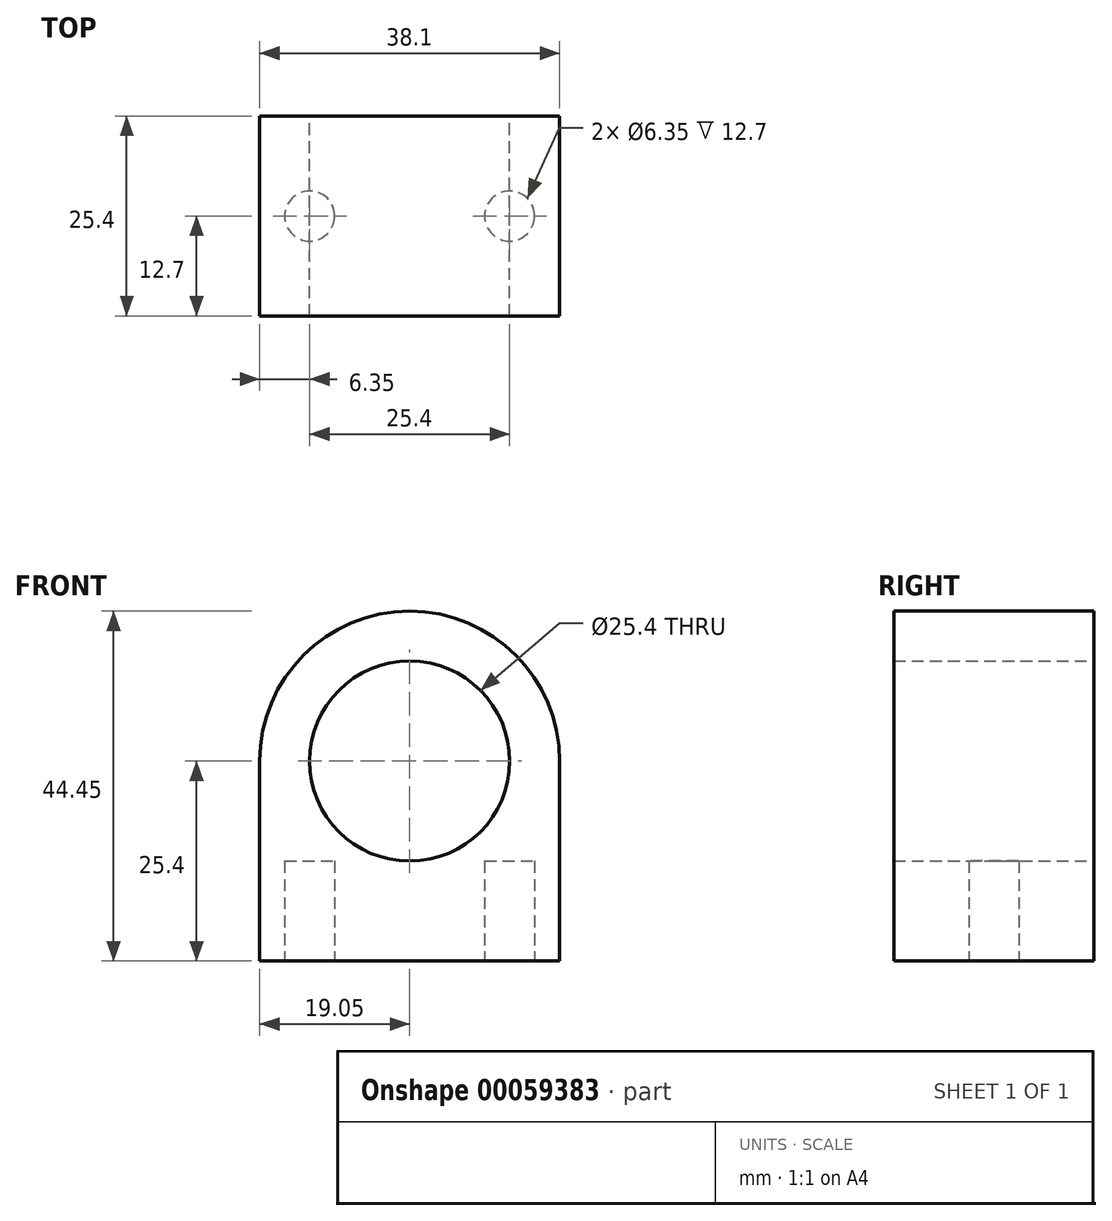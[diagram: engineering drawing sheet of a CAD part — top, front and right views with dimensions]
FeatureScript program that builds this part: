
annotation { "Feature Type Name" : "Feature", "Feature Type Description" : "" }
export const myFeature = defineFeature(function(context is Context, id is Id, definition is map)
    precondition{}
    {
        {
            var Q0;
            Q0=qCreatedBy(makeId("Front.planeOp"),FACE);
            var sketch = newSketch(context, id + "F0", { "sketchPlane" : qUnion([Q0])});
            skLineSegment(sketch, "E0", {"start": v(-52.87, 0) * mm, "end": v(-19.05, 0) * mm, "construction": true});
            skLineSegment(sketch, "E1", {"start": v(0, 60.55) * mm, "end": v(0, -55.86) * mm, "construction": true});
            skCircle(sketch, "E2", {"center": v(0, 25.4) * mm, "radius": 12.7 * mm});
            skArc(sketch, "E3", {"start": v(19.05, 25.4) * mm, "mid": v(0, 44.45) * mm, "end": v(-19.05, 25.4) * mm});
            skLineSegment(sketch, "E4", {"start": v(-19.05, 25.4) * mm, "end": v(-19.05, 0) * mm});
            skLineSegment(sketch, "E5", {"start": v(19.05, 25.4) * mm, "end": v(19.05, 0) * mm});
            skLineSegment(sketch, "E6.trimOffspring", {"start": v(0, 0) * mm, "end": v(57.82, 0) * mm, "construction": true});
            skLineSegment(sketch, "E7", {"start": v(-19.05, 0) * mm, "end": v(19.05, 0) * mm});
            skSolve(sketch);
        }
        {
            var Q0;
            Q0=makeQuery(id+"F0.imprint","IMPRINT",FACE,{"disambiguationData":[TD([[makeQuery(id+"F0.imprint","IMPRINT",EDGE,{"derivedFrom":sQuery(id+"F0.wireOp",EDGE,"E2")}),-1.0]])]});
            extrude(context, id + "F1", {"entities" : qUnion([Q0]), "endBound" : BoundingType.SYMMETRIC, "depth" : 25.4 * mm});
        }
        {
            var Q0;
            Q0=makeQuery(id+"F1.opExtrude","SWEPT_FACE",FACE,{"disambiguationData":[OSD([sQuery(id+"F0.wireOp",EDGE,"E7")])]});
            var sketch = newSketch(context, id + "F2", { "sketchPlane" : qUnion([Q0])});
            skLineSegment(sketch, "E8", {"start": v(-75.31, 0) * mm, "end": v(91.8, 0) * mm, "construction": true});
            skLineSegment(sketch, "E9", {"start": v(0, 65.82) * mm, "end": v(0, -65.5) * mm, "construction": true});
            skLineSegment(sketch, "E10", {"start": v(-12.7, 41.23) * mm, "end": v(-12.7, -51.82) * mm, "construction": true});
            skLineSegment(sketch, "E11", {"start": v(12.7, 41.23) * mm, "end": v(12.7, -51.82) * mm, "construction": true});
            skCircle(sketch, "E12", {"center": v(12.7, 0) * mm, "radius": 3.18 * mm});
            skCircle(sketch, "E13", {"center": v(-12.7, 0) * mm, "radius": 3.18 * mm});
            skSolve(sketch);
        }
        {
            var Q0;
            Q0=makeQuery(id+"F2.imprint","IMPRINT",FACE,{"disambiguationData":[TD([[makeQuery(id+"F2.imprint","IMPRINT",EDGE,{"derivedFrom":sQuery(id+"F2.wireOp",EDGE,"E13")}),1.0]])]});
            var Q1;
            Q1=makeQuery(id+"F2.imprint","IMPRINT",FACE,{"disambiguationData":[TD([[makeQuery(id+"F2.imprint","IMPRINT",EDGE,{"derivedFrom":sQuery(id+"F2.wireOp",EDGE,"E12")}),1.0]])]});
            extrude(context, id + "F3", {"entities" : qUnion([Q0, Q1]), "operationType" : NewBodyOperationType.REMOVE, "oppositeDirection" : true, "depth" : 12.7 * mm});
        }
    });
